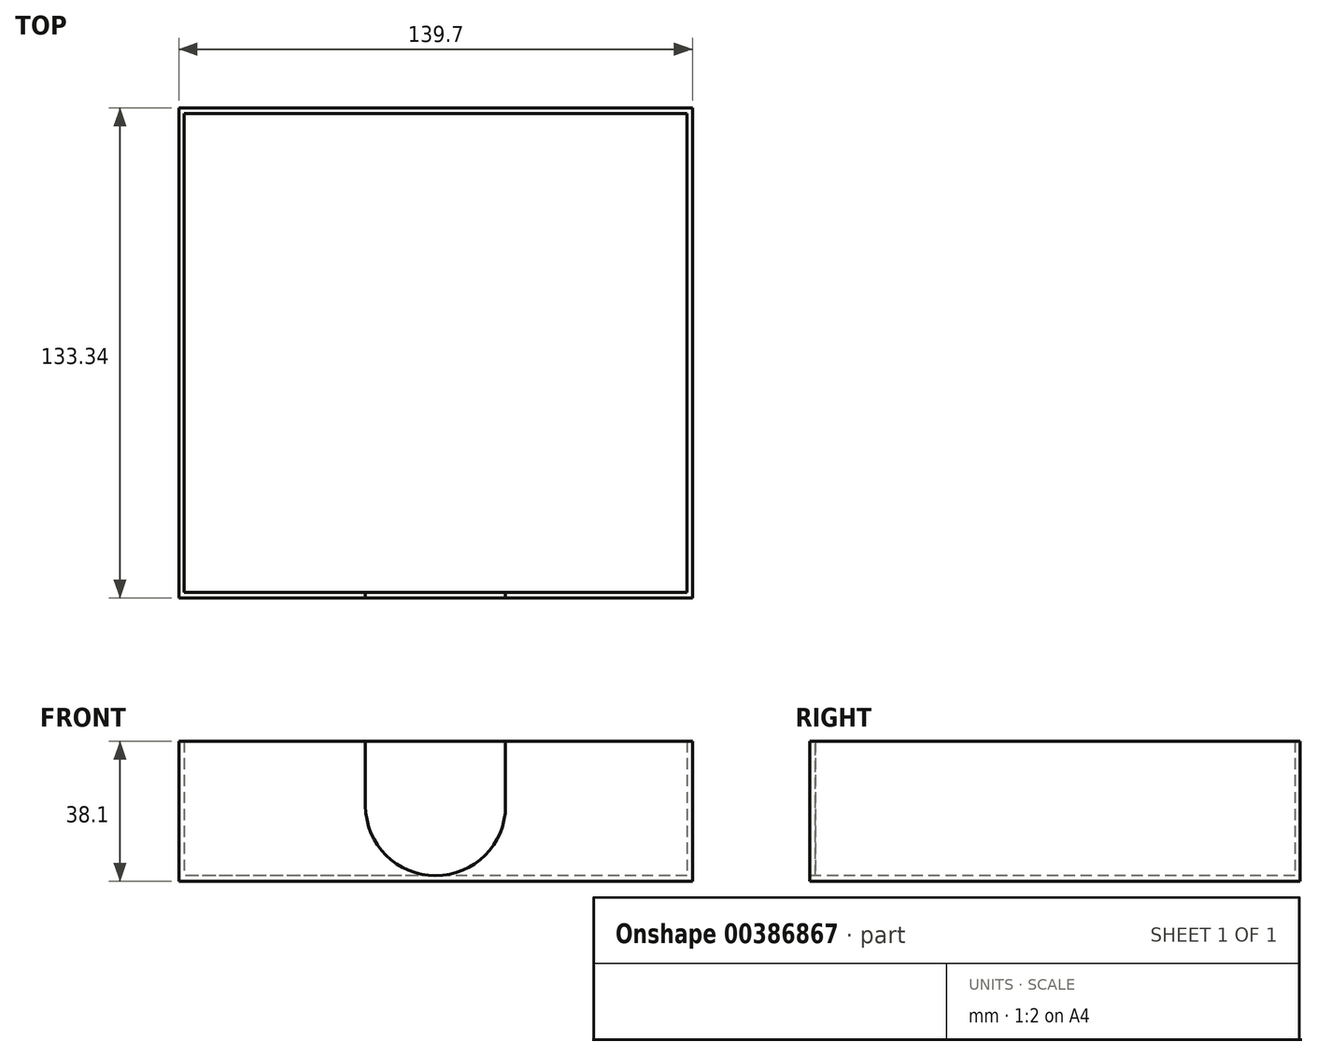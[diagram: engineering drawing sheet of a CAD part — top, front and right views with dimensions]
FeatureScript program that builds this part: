
annotation { "Feature Type Name" : "Feature", "Feature Type Description" : "" }
export const myFeature = defineFeature(function(context is Context, id is Id, definition is map)
    precondition{}
    {
        {
            var Q0;
            Q0=qCreatedBy(makeId("Top.planeOp"),FACE);
            var sketch = newSketch(context, id + "F0", { "sketchPlane" : qUnion([Q0])});
            skLineSegment(sketch, "E0.bottom", {"start": v(69.85, 66.67) * mm, "end": v(-69.85, 66.67) * mm});
            skLineSegment(sketch, "E0.top", {"start": v(69.85, -66.68) * mm, "end": v(-69.85, -66.68) * mm});
            skLineSegment(sketch, "E0.left", {"start": v(69.85, 66.67) * mm, "end": v(69.85, -66.68) * mm});
            skLineSegment(sketch, "E0.right", {"start": v(-69.85, 66.67) * mm, "end": v(-69.85, -66.68) * mm});
            skPoint(sketch, "E0.middle", {"position": v(0, 0) * mm});
            skSolve(sketch);
        }
        {
            var Q0;
            Q0=makeQuery(id+"F0.imprint","IMPRINT",FACE,{"disambiguationData":[TD([[makeQuery(id+"F0.imprint","IMPRINT",EDGE,{"derivedFrom":sQuery(id+"F0.wireOp",EDGE,"E0.bottom")}),1.0]])]});
            extrude(context, id + "F1", {"entities" : qUnion([Q0]), "depth" : 38.1 * mm});
        }
        {
            var Q0;
            Q0=makeQuery(id+"F1.opExtrude","CAP_FACE",FACE,{"disambiguationData":[OSD([sQuery(id+"F0.wireOp",EDGE,"E0.bottom"),sQuery(id+"F0.wireOp",EDGE,"E0.top"),sQuery(id+"F0.wireOp",EDGE,"E0.left"),sQuery(id+"F0.wireOp",EDGE,"E0.right")])],"isStart":false});
            shell(context, id + "F2", {"entities" : qUnion([Q0]), "thickness" : 1.5 * mm});
        }
        {
            var Q0;
            Q0=makeQuery(id+"F1.opExtrude","SWEPT_FACE",FACE,{"disambiguationData":[OSD([sQuery(id+"F0.wireOp",EDGE,"E0.top")])]});
            var sketch = newSketch(context, id + "F3", { "sketchPlane" : qUnion([Q0])});
            skCircle(sketch, "E1", {"center": v(0, 20.55) * mm, "radius": 19.05 * mm});
            skPoint(sketch, "E1.centerSnap0", {"position": v(0, 0) * mm});
            skLineSegment(sketch, "E2.bottom", {"start": v(19.05, 20.55) * mm, "end": v(-19.05, 20.55) * mm});
            skLineSegment(sketch, "E2.top", {"start": v(19.05, 38.1) * mm, "end": v(-19.05, 38.1) * mm});
            skLineSegment(sketch, "E2.left", {"start": v(19.05, 20.55) * mm, "end": v(19.05, 38.1) * mm});
            skLineSegment(sketch, "E2.right", {"start": v(-19.05, 20.55) * mm, "end": v(-19.05, 38.1) * mm});
            skSolve(sketch);
        }
        {
            var Q0;
            Q0 = qSketchRegion(id + "F3", true);
            extrude(context, id + "F4", {"entities" : qUnion([Q0]), "operationType" : NewBodyOperationType.REMOVE, "oppositeDirection" : true, "depth" : 1.5 * mm, "offsetDistance" : 25.4 * mm});
        }
    });
